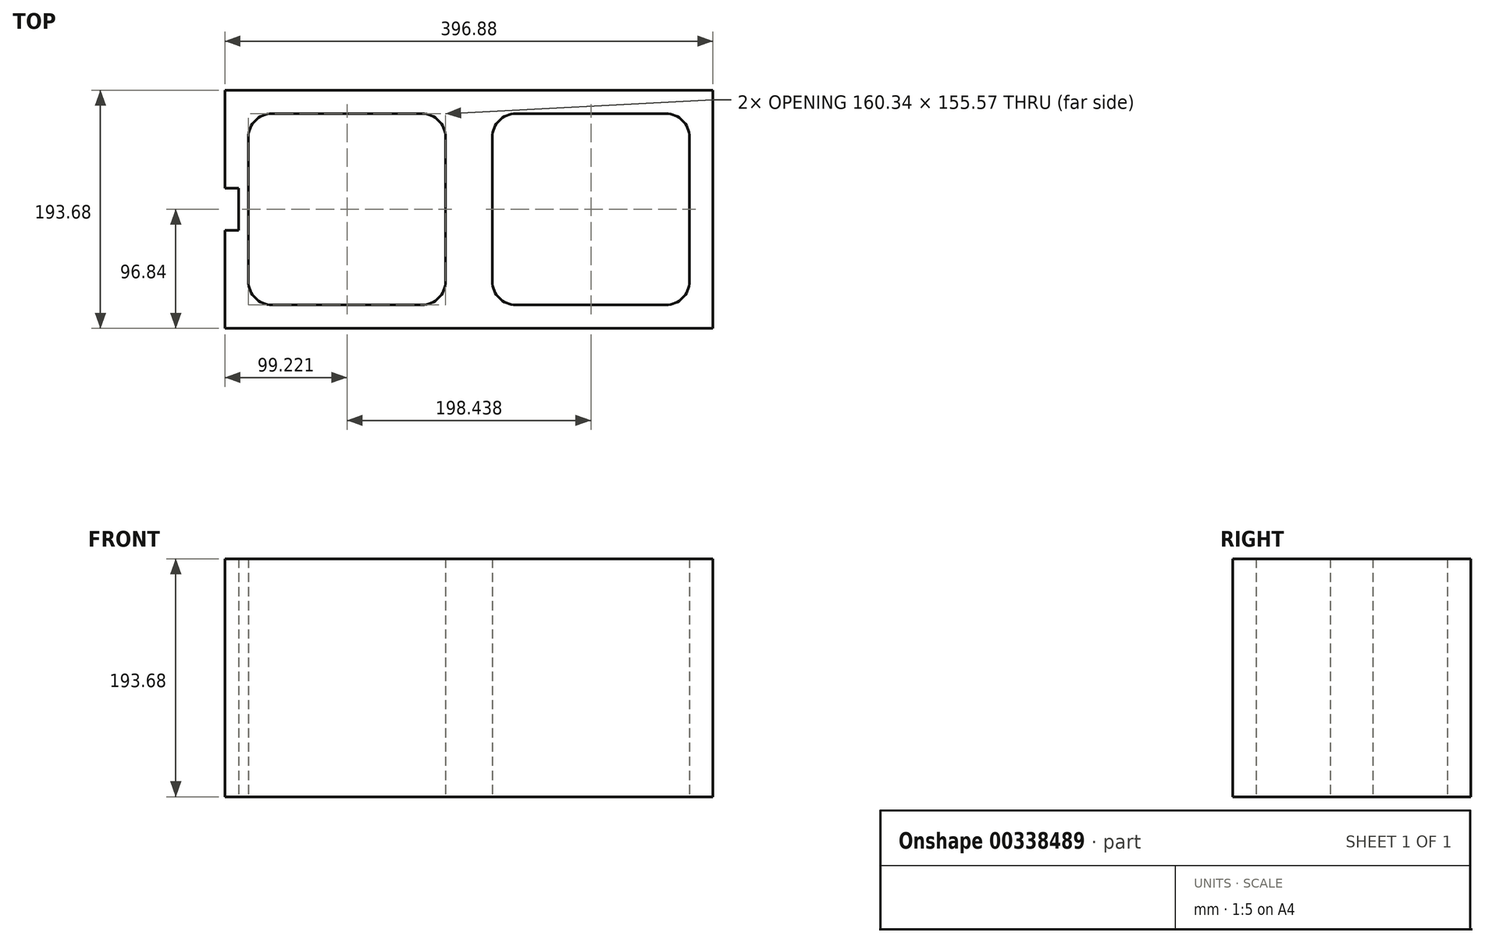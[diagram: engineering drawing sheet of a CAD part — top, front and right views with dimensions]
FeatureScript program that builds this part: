
annotation { "Feature Type Name" : "Feature", "Feature Type Description" : "" }
export const myFeature = defineFeature(function(context is Context, id is Id, definition is map)
    precondition{}
    {
        {
            var Q0;
            Q0=qCreatedBy(makeId("Top.planeOp"),FACE);
            var sketch = newSketch(context, id + "F0", { "sketchPlane" : qUnion([Q0])});
            skLineSegment(sketch, "E0.left", {"start": v(-198.44, 96.84) * mm, "end": v(-198.44, 17.27) * mm});
            skLineSegment(sketch, "E0.right", {"start": v(198.44, 96.84) * mm, "end": v(198.44, -96.84) * mm});
            skPoint(sketch, "E0.middle", {"position": v(0, 0) * mm});
            skLineSegment(sketch, "E1", {"start": v(-187.35, -17.27) * mm, "end": v(-198.44, -17.27) * mm});
            skLineSegment(sketch, "E2", {"start": v(-187.35, 17.27) * mm, "end": v(-198.44, 17.27) * mm});
            skLineSegment(sketch, "E3.trimOffspring", {"start": v(-198.44, -17.27) * mm, "end": v(-198.44, -96.84) * mm});
            skLineSegment(sketch, "E4", {"start": v(0, 96.84) * mm, "end": v(0, -96.84) * mm});
            skLineSegment(sketch, "E5", {"start": v(198.44, 96.84) * mm, "end": v(0, 96.84) * mm});
            skLineSegment(sketch, "E6", {"start": v(0, 96.84) * mm, "end": v(-198.44, 96.84) * mm});
            skLineSegment(sketch, "E7", {"start": v(198.44, -96.84) * mm, "end": v(0, -96.84) * mm});
            skLineSegment(sketch, "E8", {"start": v(0, -96.84) * mm, "end": v(-198.44, -96.84) * mm});
            skLineSegment(sketch, "E9.0", {"start": v(179.39, 77.79) * mm, "end": v(19.05, 77.79) * mm});
            skLineSegment(sketch, "E9.1", {"start": v(179.39, 77.79) * mm, "end": v(179.39, -77.79) * mm});
            skLineSegment(sketch, "E9.2", {"start": v(179.39, -77.79) * mm, "end": v(19.05, -77.79) * mm});
            skLineSegment(sketch, "E9.3", {"start": v(19.05, 77.79) * mm, "end": v(19.05, -77.79) * mm});
            skLineSegment(sketch, "E10.0", {"start": v(-19.05, 77.79) * mm, "end": v(-19.05, -77.79) * mm});
            skLineSegment(sketch, "E10.1", {"start": v(-19.05, -77.79) * mm, "end": v(-179.39, -77.79) * mm});
            skLineSegment(sketch, "E10.2", {"start": v(-19.05, 77.79) * mm, "end": v(-179.39, 77.79) * mm});
            skLineSegment(sketch, "E11", {"start": v(-187.35, -17.27) * mm, "end": v(-187.35, 17.27) * mm});
            skLineSegment(sketch, "E12", {"start": v(-179.39, -77.79) * mm, "end": v(-179.39, 77.79) * mm});
            skSolve(sketch);
        }
        {
            var Q0;
            Q0=makeQuery(id+"F0.imprint","IMPRINT",FACE,{"disambiguationData":[TD([[makeQuery(id+"F0.imprint","IMPRINT",EDGE,{"derivedFrom":sQuery(id+"F0.wireOp",EDGE,"E0.right")}),-1.0]])]});
            var Q1;
            Q1=makeQuery(id+"F0.imprint","IMPRINT",FACE,{"disambiguationData":[TD([[makeQuery(id+"F0.imprint","IMPRINT",EDGE,{"derivedFrom":sQuery(id+"F0.wireOp",EDGE,"E0.left")}),1.0]])]});
            extrude(context, id + "F1", {"entities" : qUnion([Q0, Q1]), "depth" : 193.67 * mm});
        }
        {
            var Q0;
            Q0=makeQuery(id+"F1.opExtrude","SWEPT_EDGE",EDGE,{"disambiguationData":[OSD([sQuery(id+"F0.wireOp",EDGE,"E9.0"),sQuery(id+"F0.wireOp",EDGE,"E9.1")])]});
            var Q1;
            Q1=makeQuery(id+"F1.opExtrude","SWEPT_EDGE",EDGE,{"disambiguationData":[OSD([sQuery(id+"F0.wireOp",EDGE,"E9.1"),sQuery(id+"F0.wireOp",EDGE,"E9.2")])]});
            var Q2;
            Q2=makeQuery(id+"F1.opExtrude","SWEPT_EDGE",EDGE,{"disambiguationData":[OSD([sQuery(id+"F0.wireOp",EDGE,"E9.0"),sQuery(id+"F0.wireOp",EDGE,"E9.3")])]});
            var Q3;
            Q3=makeQuery(id+"F1.opExtrude","SWEPT_EDGE",EDGE,{"disambiguationData":[OSD([sQuery(id+"F0.wireOp",EDGE,"E9.2"),sQuery(id+"F0.wireOp",EDGE,"E9.3")])]});
            var Q4;
            Q4=makeQuery(id+"F1.opExtrude","SWEPT_EDGE",EDGE,{"disambiguationData":[OSD([sQuery(id+"F0.wireOp",EDGE,"E10.0"),sQuery(id+"F0.wireOp",EDGE,"E10.2")])]});
            var Q5;
            Q5=makeQuery(id+"F1.opExtrude","SWEPT_EDGE",EDGE,{"disambiguationData":[OSD([sQuery(id+"F0.wireOp",EDGE,"E10.0"),sQuery(id+"F0.wireOp",EDGE,"E10.1")])]});
            var Q6;
            Q6=makeQuery(id+"F1.opExtrude","SWEPT_EDGE",EDGE,{"disambiguationData":[OSD([sQuery(id+"F0.wireOp",EDGE,"E10.2"),sQuery(id+"F0.wireOp",EDGE,"E12")])]});
            var Q7;
            Q7=makeQuery(id+"F1.opExtrude","SWEPT_EDGE",EDGE,{"disambiguationData":[OSD([sQuery(id+"F0.wireOp",EDGE,"E10.1"),sQuery(id+"F0.wireOp",EDGE,"E12")])]});
            fillet(context, id + "F2", {"entities" : qUnion([Q0, Q1, Q2, Q3, Q4, Q5, Q6, Q7]), "radius" : 19.05 * mm, "tangentPropagation" : true, "allowEdgeOverflow" : false});
        }
    });
